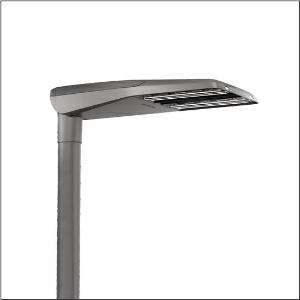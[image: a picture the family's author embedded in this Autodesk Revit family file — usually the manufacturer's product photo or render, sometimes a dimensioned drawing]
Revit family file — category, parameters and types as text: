
# Revit family: streetlight_sl_11_iq_midi___st1_2a_5xc3a51e08me_cf1e
name_source: partatom
category: Lighting Fixtures
units: mm (PartAtom-declared; Revit-internal decimal feet)

## family parameters
Cut with Voids When Loaded = No
Host = Face
Light Source = No
Part Type = Normal
Room Calculation Point = No
Round Connector Dimension = Use Diameter
Shared = No

## types (1)
- --- (1 x LED, 18110 lm, 124.7 W, 3000K)
    Apparent Load = 125 VA
    CIE Flux Codes = 32 70 96 100 100
    Color Rendering = 70
    Color Temperature = 3000K
    Default Elevation = 1800 mm
    Description = Streetlight SL 11 iQ midi, mast luminaire, primary light control with 3 zone facetted reflector, of plastic, silver coated, highly specular, primary optical cover: cover, of PMMA, transparent, light distribution: ST1.2a, light emission: direct distribution, primary light characteristic: asymmetric, installation type: post-top, side-entry, LED, High Power LED, rated luminous flux: 18.110lm, luminous efficacy: 145lm/W, light colour: 730, colour temperature: 3000K, control: optimised constant luminous flux control (CLO 2.0), Desk-Remote (wireless, voltage-free reading and setting of iQ features in the workshop via application-optimized NFC function/RFID function), Light-Fading, Smart-Wire, Night-Set, Lumen-Switch, Temp-Guard, Auto-Match, with cable H07RN-F 5x 1.5mm², mains connection: 230..240V, AC, 50/60Hz, connection cable pre-assembled, cable length: 12,5m, start of lifetime: 125W, end of service life: 132W, reduction: 57W, luminaire housing, of diecast aluminium, powder-coated, Siteco® metallic grey (DB 702S), please order mast flange separately, inclination adjustable without tools: 0°, 5°, 10°, 15° (post-top) | 0°, -5°, -10°, -15° (side-entry), sealing non-destructively replaceable, multi-level sealing system, length: 780mm, width: 376mm, height: 118mm, mast flange for spigot size: 42mm (side-entry): 5XC10008XM4, 60/48mm (side-entry/post-top): 5XC10108XM2, 76/60mm (side-entry/post-top): 5XC10108XM1, equipment: Power, protection rating (complete): IP66, insulation class (complete): insulation class II (safety insulation), certification: CE, ENEC, VDE, impact resistance: IK09, permissible operating ambient temperature for outdoor applications: -25..+50°C, standard-compliant lighting for roads and squares, Environmental Product Declaration (EPD) tested and certified by an independent institute, packaging unit: 1 piece

Light Distribution: ST1.2a
    Height = 118 mm
    Lamp = 1 x LED
    Lamp Light Flux = 18110 lm
    Lamp Power = 124.7 W
    Lamp count = 1
    Length = 780 mm
    Luminous efficacy = 145 lm/W
    Manufacturer = Siteco
    ModVariant = No
    Model = 5XC3A51E08ME
    Number of Poles = 1
    OnlyDefault = Yes
    Power Factor = 1
    Product Name = Streetlight SL 11 iQ midi | ST1.2a
    Product group = mast luminaire | pylon top
    ProductGroupID = 6100
    Protection Class = Protection class II
    Protection Degree = IP 66
    RLX_Detail_Level = 1
    RLX_Emergency_Light_Flux = 0 lm
    RLX_Emergency_Type = 0
    RLX_Emergency_Type_DB = No
    RlxData = <blob elided: 70809 chars, md5=f126a62f>
    Socket = socket
    Standby Power = 0 W
    System Light Flux = 18110 lm
    System Power = 125 W
    Type Comments = factory setting: luminous flux: 100 % | dim-lin: 254 | 557 mA
    Type Image = l_1005960.jpg
    URL = http://relux.com
    VarID = @adj_169261
    Voltage = 0 V
    Weight = 0.00 kg
    Width = 376 mm

## geometry (parser evidence)
native form markers: Blend x4, Sweep x10
no freeform markers — native parametric forms only
